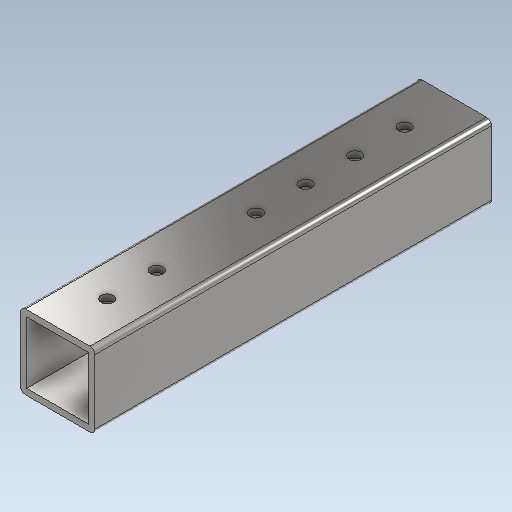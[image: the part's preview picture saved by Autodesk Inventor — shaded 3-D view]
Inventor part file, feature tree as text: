
AUTODESK INVENTOR PART (.ipt)
format: ipt  version: 2021 (Build 250183000, 183)  size: 236,544 bytes
history: native  units: mm
features: sketch x3, hole x2, extrude x1, fillet x1, plane x1, split x1, pattern_linear x1
ambient origin geometry x8: Origin, YZ Plane, XZ Plane, XY Plane, X Axis, Y Axis, Z Axis, Center Point
bodies: Solid1 (feature_tree)
feature tree (10):
  extrude  "Extrusion1"  Depth=30.0mm
  fillet  "Fillet1"  Radius=15.0mm
  plane  "Work Plane1"
  split  "Split1"
  hole  "Hole1"  [1 undecoded]
  pattern_linear  "Rectangular Pattern1"  Count1=100 Spacing1=0.0mm
  hole  "Hole2"  [1 undecoded]
  sketch  "Sketch1"  dims[d0=30.0mm d1=30.0mm d2=15.0mm]
  sketch  "Sketch2"  dims[d3=15.0mm d4=2.5mm d5=1000.0mm d6=0.0mm]
  sketch  "Sketch3"  dims[d7=2.0mm d8=-160.0mm d9=0.0mm d10=20.0mm d11=5.0mm d12=6.0mm d13=4.0mm d14=2.0mm d15=90.0deg d16=8.0mm d17=20.594885mm d18=40.0mm d20=20.0mm d21=20.0mm d22=0.0mm d23=5.0mm d24=6.0mm d25=4.0mm d26=2.0mm d27=90.0deg d28=8.0mm d29=20.594885mm d30=0.0mm d31=20.0mm]
note: 2 required parameter values undecoded (feature->parameter linkage not recoverable at this tier; creation-order binding heuristic only, values carry confidence <= 0.55)
